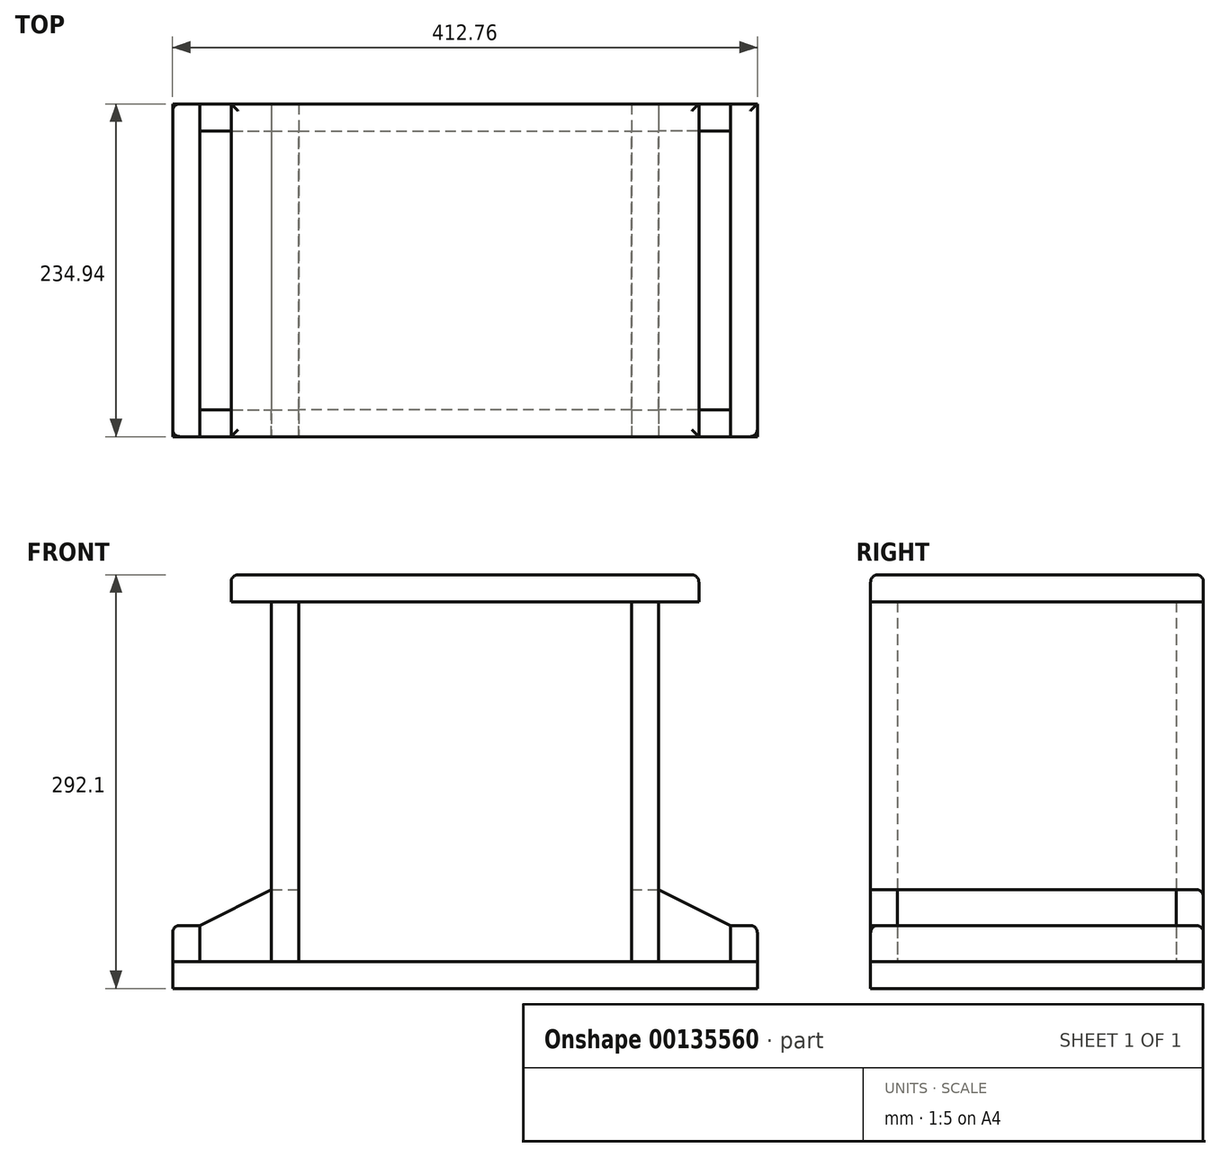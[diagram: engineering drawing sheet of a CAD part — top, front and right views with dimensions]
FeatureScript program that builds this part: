
annotation { "Feature Type Name" : "Feature", "Feature Type Description" : "" }
export const myFeature = defineFeature(function(context is Context, id is Id, definition is map)
    precondition{}
    {
        {
            var Q0;
            Q0=qCreatedBy(makeId("Top.planeOp"),FACE);
            var sketch = newSketch(context, id + "F0", { "sketchPlane" : qUnion([Q0])});
            skLineSegment(sketch, "E0.bottom", {"start": v(206.38, -117.47) * mm, "end": v(-206.38, -117.48) * mm});
            skLineSegment(sketch, "E0.top", {"start": v(206.38, 117.48) * mm, "end": v(-206.38, 117.47) * mm});
            skLineSegment(sketch, "E0.left", {"start": v(206.38, -117.47) * mm, "end": v(206.38, 117.48) * mm});
            skLineSegment(sketch, "E0.right", {"start": v(-206.38, -117.48) * mm, "end": v(-206.38, 117.48) * mm});
            skPoint(sketch, "E0.middle", {"position": v(0, 0) * mm});
            skSolve(sketch);
        }
        {
            var Q0;
            Q0 = qSketchRegion(id + "F0", true);
            extrude(context, id + "F1", {"entities" : qUnion([Q0]), "depth" : 19.05 * mm});
        }
        {
            var Q0;
            Q0=makeQuery(id+"F1.opExtrude","CAP_FACE",FACE,{"disambiguationData":[OSD([sQuery(id+"F0.wireOp",EDGE,"E0.bottom"),sQuery(id+"F0.wireOp",EDGE,"E0.top"),sQuery(id+"F0.wireOp",EDGE,"E0.left"),sQuery(id+"F0.wireOp",EDGE,"E0.right")])],"isStart":false});
            var sketch = newSketch(context, id + "F2", { "sketchPlane" : qUnion([Q0])});
            skLineSegment(sketch, "E1.bottom", {"start": v(-206.38, 117.48) * mm, "end": v(-187.33, 117.48) * mm});
            skLineSegment(sketch, "E1.top", {"start": v(-206.38, -117.48) * mm, "end": v(-187.33, -117.48) * mm});
            skLineSegment(sketch, "E1.left", {"start": v(-206.38, 117.48) * mm, "end": v(-206.38, -117.48) * mm});
            skLineSegment(sketch, "E1.right", {"start": v(-187.33, 117.48) * mm, "end": v(-187.33, -117.48) * mm});
            skLineSegment(sketch, "E2.bottom", {"start": v(206.38, 117.48) * mm, "end": v(187.33, 117.48) * mm});
            skLineSegment(sketch, "E2.top", {"start": v(206.38, -117.47) * mm, "end": v(187.33, -117.47) * mm});
            skLineSegment(sketch, "E2.left", {"start": v(206.38, 117.48) * mm, "end": v(206.38, -117.47) * mm});
            skLineSegment(sketch, "E2.right", {"start": v(187.33, 117.48) * mm, "end": v(187.33, -117.47) * mm});
            skSolve(sketch);
        }
        {
            var Q0;
            Q0 = qSketchRegion(id + "F2", true);
            extrude(context, id + "F3", {"entities" : qUnion([Q0]), "depth" : 25.4 * mm});
        }
        {
            var Q0;
            Q0=makeQuery(id+"F1.opExtrude","CAP_FACE",FACE,{"disambiguationData":[OSD([sQuery(id+"F0.wireOp",EDGE,"E0.bottom"),sQuery(id+"F0.wireOp",EDGE,"E0.top"),sQuery(id+"F0.wireOp",EDGE,"E0.left"),sQuery(id+"F0.wireOp",EDGE,"E0.right")])],"isStart":false});
            var sketch = newSketch(context, id + "F4", { "sketchPlane" : qUnion([Q0])});
            skLineSegment(sketch, "E3.bottom", {"start": v(-187.33, 117.47) * mm, "end": v(-136.53, 117.47) * mm});
            skLineSegment(sketch, "E3.top", {"start": v(-187.33, 98.42) * mm, "end": v(-136.53, 98.42) * mm});
            skLineSegment(sketch, "E3.left", {"start": v(-187.33, 117.47) * mm, "end": v(-187.33, 98.42) * mm});
            skLineSegment(sketch, "E3.right", {"start": v(-136.53, 117.47) * mm, "end": v(-136.53, 98.42) * mm});
            skLineSegment(sketch, "E4.bottom", {"start": v(-187.33, -117.48) * mm, "end": v(-136.53, -117.48) * mm});
            skLineSegment(sketch, "E4.top", {"start": v(-187.33, -98.43) * mm, "end": v(-136.53, -98.43) * mm});
            skLineSegment(sketch, "E4.left", {"start": v(-187.33, -117.48) * mm, "end": v(-187.33, -98.43) * mm});
            skLineSegment(sketch, "E4.right", {"start": v(-136.53, -117.48) * mm, "end": v(-136.53, -98.43) * mm});
            skSolve(sketch);
        }
        {
            var Q0;
            Q0 = qSketchRegion(id + "F4", true);
            extrude(context, id + "F5", {"entities" : qUnion([Q0]), "depth" : 50.8 * mm});
        }
        {
            var Q0;
            Q0=makeQuery(id+"F1.opExtrude","CAP_FACE",FACE,{"disambiguationData":[OSD([sQuery(id+"F0.wireOp",EDGE,"E0.bottom"),sQuery(id+"F0.wireOp",EDGE,"E0.top"),sQuery(id+"F0.wireOp",EDGE,"E0.left"),sQuery(id+"F0.wireOp",EDGE,"E0.right")])],"isStart":false});
            var sketch = newSketch(context, id + "F6", { "sketchPlane" : qUnion([Q0])});
            skLineSegment(sketch, "E5.bottom", {"start": v(-136.53, 117.48) * mm, "end": v(-117.48, 117.48) * mm});
            skLineSegment(sketch, "E5.top", {"start": v(-136.53, -117.48) * mm, "end": v(-117.48, -117.48) * mm});
            skLineSegment(sketch, "E5.left", {"start": v(-136.53, 117.48) * mm, "end": v(-136.53, -117.48) * mm});
            skLineSegment(sketch, "E5.right", {"start": v(-117.48, 117.48) * mm, "end": v(-117.48, -117.48) * mm});
            skLineSegment(sketch, "E6.bottom", {"start": v(136.53, 117.48) * mm, "end": v(117.48, 117.48) * mm});
            skLineSegment(sketch, "E6.top", {"start": v(136.53, -117.47) * mm, "end": v(117.48, -117.47) * mm});
            skLineSegment(sketch, "E6.left", {"start": v(136.53, 117.48) * mm, "end": v(136.53, -117.47) * mm});
            skLineSegment(sketch, "E6.right", {"start": v(117.48, 117.48) * mm, "end": v(117.48, -117.47) * mm});
            skSolve(sketch);
        }
        {
            var Q0;
            Q0 = qSketchRegion(id + "F6", true);
            extrude(context, id + "F7", {"entities" : qUnion([Q0]), "depth" : 254 * mm});
        }
        {
            var Q0;
            Q0=makeQuery(id+"F7.opExtrude","SWEPT_FACE",FACE,{"disambiguationData":[OSD([sQuery(id+"F6.wireOp",EDGE,"E6.left")])]});
            var sketch = newSketch(context, id + "F8", { "sketchPlane" : qUnion([Q0])});
            skLineSegment(sketch, "E7.bottom", {"start": v(-98.43, 19.05) * mm, "end": v(98.42, 19.05) * mm});
            skLineSegment(sketch, "E7.top", {"start": v(-98.43, 69.85) * mm, "end": v(98.42, 69.85) * mm});
            skLineSegment(sketch, "E7.left", {"start": v(-98.43, 19.05) * mm, "end": v(-98.43, 69.85) * mm});
            skLineSegment(sketch, "E7.right", {"start": v(98.42, 19.05) * mm, "end": v(98.42, 69.85) * mm});
            skSolve(sketch);
        }
        {
            var Q0;
            Q0 = qSketchRegion(id + "F8", true);
            var Q1;
            Q1=makeQuery(id+"F7.opExtrude","SWEPT_FACE",FACE,{"disambiguationData":[OSD([sQuery(id+"F6.wireOp",EDGE,"E5.left")])]});
            extrude(context, id + "F9", {"entities" : qUnion([Q0]), "operationType" : NewBodyOperationType.REMOVE, "endBound" : BoundingType.UP_TO_SURFACE, "oppositeDirection" : true, "endBoundEntityFace" : qUnion([Q1]), "depth" : 25.4 * mm});
        }
        {
            var Q0;
            Q0=makeQuery(id+"F1.opExtrude","CAP_FACE",FACE,{"disambiguationData":[OSD([sQuery(id+"F0.wireOp",EDGE,"E0.bottom"),sQuery(id+"F0.wireOp",EDGE,"E0.top"),sQuery(id+"F0.wireOp",EDGE,"E0.left"),sQuery(id+"F0.wireOp",EDGE,"E0.right")])],"isStart":false});
            var sketch = newSketch(context, id + "F10", { "sketchPlane" : qUnion([Q0])});
            skLineSegment(sketch, "E8.bottom", {"start": v(-117.48, 117.48) * mm, "end": v(117.47, 117.48) * mm});
            skLineSegment(sketch, "E8.top", {"start": v(-117.48, 98.43) * mm, "end": v(117.47, 98.43) * mm});
            skLineSegment(sketch, "E8.left", {"start": v(-117.48, 117.48) * mm, "end": v(-117.48, 98.43) * mm});
            skLineSegment(sketch, "E8.right", {"start": v(117.47, 117.48) * mm, "end": v(117.47, 98.43) * mm});
            skLineSegment(sketch, "E9.bottom", {"start": v(117.47, -117.47) * mm, "end": v(-117.48, -117.48) * mm});
            skLineSegment(sketch, "E9.top", {"start": v(117.47, -98.42) * mm, "end": v(-117.48, -98.43) * mm});
            skLineSegment(sketch, "E9.left", {"start": v(117.47, -117.47) * mm, "end": v(117.47, -98.42) * mm});
            skLineSegment(sketch, "E9.right", {"start": v(-117.48, -117.48) * mm, "end": v(-117.48, -98.43) * mm});
            skSolve(sketch);
        }
        {
            var Q0;
            Q0 = qSketchRegion(id + "F10", true);
            extrude(context, id + "F11", {"entities" : qUnion([Q0]), "depth" : 254 * mm});
        }
        {
            var Q0;
            Q0=makeQuery(id+"F11.opExtrude","CAP_FACE",FACE,{"disambiguationData":[OSD([sQuery(id+"F10.wireOp",EDGE,"E8.bottom"),sQuery(id+"F10.wireOp",EDGE,"E8.top"),sQuery(id+"F10.wireOp",EDGE,"E8.left"),sQuery(id+"F10.wireOp",EDGE,"E8.right")])],"isStart":false});
            var sketch = newSketch(context, id + "F12", { "sketchPlane" : qUnion([Q0])});
            skLineSegment(sketch, "E10.bottom", {"start": v(165.1, -117.48) * mm, "end": v(-165.1, -117.48) * mm});
            skLineSegment(sketch, "E10.top", {"start": v(165.1, 117.48) * mm, "end": v(-165.1, 117.48) * mm});
            skLineSegment(sketch, "E10.left", {"start": v(165.1, -117.48) * mm, "end": v(165.1, 117.48) * mm});
            skLineSegment(sketch, "E10.right", {"start": v(-165.1, -117.48) * mm, "end": v(-165.1, 117.48) * mm});
            skPoint(sketch, "E10.middle", {"position": v(0, 0) * mm});
            skSolve(sketch);
        }
        {
            var Q0;
            Q0 = qSketchRegion(id + "F12", true);
            extrude(context, id + "F13", {"entities" : qUnion([Q0]), "depth" : 19.05 * mm});
        }
        {
            var Q0;
            Q0=makeQuery(id+"F5.opExtrude","SWEPT_FACE",FACE,{"disambiguationData":[OSD([sQuery(id+"F4.wireOp",EDGE,"E4.bottom")])]});
            var sketch = newSketch(context, id + "F14", { "sketchPlane" : qUnion([Q0])});
            skLineSegment(sketch, "E11", {"start": v(-136.53, 69.85) * mm, "end": v(-187.33, 44.45) * mm});
            skLineSegment(sketch, "E12", {"start": v(-187.33, 44.45) * mm, "end": v(-187.33, 69.85) * mm});
            skLineSegment(sketch, "E13", {"start": v(-187.33, 69.85) * mm, "end": v(-136.53, 69.85) * mm});
            skSolve(sketch);
        }
        {
            var Q0;
            Q0 = qSketchRegion(id + "F14", true);
            extrude(context, id + "F15", {"entities" : qUnion([Q0]), "operationType" : NewBodyOperationType.REMOVE, "endBound" : BoundingType.THROUGH_ALL, "oppositeDirection" : true, "depth" : 25.4 * mm});
        }
        {
            var Q0;
            Q0=makeQuery(id+"F3.opExtrude","CAP_EDGE",EDGE,{"disambiguationData":[OSD([sQuery(id+"F2.wireOp",EDGE,"E1.left")])],"isStart":false});
            var Q1;
            Q1=makeQuery(id+"F3.opExtrude","CAP_EDGE",EDGE,{"disambiguationData":[OSD([sQuery(id+"F2.wireOp",EDGE,"E2.left")])],"isStart":false});
            var Q2;
            Q2=makeQuery(id+"F3.opExtrude","CAP_EDGE",EDGE,{"disambiguationData":[OSD([sQuery(id+"F2.wireOp",EDGE,"E2.bottom")])],"isStart":false});
            var Q3;
            Q3=makeQuery(id+"F3.opExtrude","CAP_EDGE",EDGE,{"disambiguationData":[OSD([sQuery(id+"F2.wireOp",EDGE,"E1.bottom")])],"isStart":false});
            var Q4;
            Q4=makeQuery(id+"F3.opExtrude","SWEPT_EDGE",EDGE,{"disambiguationData":[OSD([sQuery(id+"F2.wireOp",EDGE,"E1.top"),sQuery(id+"F2.wireOp",EDGE,"E1.left")])]});
            var Q5;
            Q5=makeQuery(id+"F3.opExtrude","SWEPT_EDGE",EDGE,{"disambiguationData":[OSD([sQuery(id+"F2.wireOp",EDGE,"E1.bottom"),sQuery(id+"F2.wireOp",EDGE,"E1.left")])]});
            var Q6;
            Q6=makeQuery(id+"F3.opExtrude","SWEPT_EDGE",EDGE,{"disambiguationData":[OSD([sQuery(id+"F2.wireOp",EDGE,"E2.top"),sQuery(id+"F2.wireOp",EDGE,"E2.left")])]});
            var Q7;
            Q7=makeQuery(id+"F3.opExtrude","CAP_EDGE",EDGE,{"disambiguationData":[OSD([sQuery(id+"F2.wireOp",EDGE,"E2.top")])],"isStart":false});
            var Q8;
            Q8=makeQuery(id+"F3.opExtrude","CAP_EDGE",EDGE,{"disambiguationData":[OSD([sQuery(id+"F2.wireOp",EDGE,"E1.top")])],"isStart":false});
            var Q9;
            Q9=makeQuery(id+"F15.boolean.opBoolean","INTERSECT",EDGE,{"derivedFrom":[makeQuery(id+"F5.opExtrude","SWEPT_FACE",FACE,{"disambiguationData":[OSD([sQuery(id+"F4.wireOp",EDGE,"E3.bottom")])]}),makeQuery(id+"F15.opExtrude","SWEPT_FACE",FACE,{"disambiguationData":[OSD([sQuery(id+"F14.wireOp",EDGE,"E11")])]})]});
            var Q10;
            Q10=makeQuery(id+"F15.boolean.opBoolean","COPY",EDGE,{"derivedFrom":makeQuery(id+"F15.opExtrude","CAP_EDGE",EDGE,{"disambiguationData":[OSD([sQuery(id+"F14.wireOp",EDGE,"E11")])],"isStart":true})});
            var Q11;
            Q11=makeQuery(id+"F13.opExtrude","CAP_EDGE",EDGE,{"disambiguationData":[OSD([sQuery(id+"F12.wireOp",EDGE,"E10.top")])],"isStart":false});
            var Q12;
            Q12=makeQuery(id+"F13.opExtrude","CAP_EDGE",EDGE,{"disambiguationData":[OSD([sQuery(id+"F12.wireOp",EDGE,"E10.right")])],"isStart":false});
            var Q13;
            Q13=makeQuery(id+"F13.opExtrude","CAP_EDGE",EDGE,{"disambiguationData":[OSD([sQuery(id+"F12.wireOp",EDGE,"E10.bottom")])],"isStart":false});
            var Q14;
            Q14=makeQuery(id+"F13.opExtrude","CAP_EDGE",EDGE,{"disambiguationData":[OSD([sQuery(id+"F12.wireOp",EDGE,"E10.left")])],"isStart":false});
            fillet(context, id + "F16", {"entities" : qUnion([Q0, Q1, Q2, Q3, Q4, Q5, Q6, Q7, Q8, Q9, Q10, Q11, Q12, Q13, Q14]), "radius" : 5.08 * mm, "tangentPropagation" : true, "allowEdgeOverflow" : false});
        }
        {
            var Q0;
            Q0=makeQuery(id+"F5.opExtrude","SWEPT_BODY",BODY,{"disambiguationData":[OSD([sQuery(id+"F4.wireOp",EDGE,"E4.bottom"),sQuery(id+"F4.wireOp",EDGE,"E4.top"),sQuery(id+"F4.wireOp",EDGE,"E4.left"),sQuery(id+"F4.wireOp",EDGE,"E4.right")])]});
            var Q1;
            Q1=makeQuery(id+"F5.opExtrude","SWEPT_BODY",BODY,{"disambiguationData":[OSD([sQuery(id+"F4.wireOp",EDGE,"E3.bottom"),sQuery(id+"F4.wireOp",EDGE,"E3.top"),sQuery(id+"F4.wireOp",EDGE,"E3.left"),sQuery(id+"F4.wireOp",EDGE,"E3.right")])]});
            var Q2;
            Q2=qCreatedBy(makeId("Right.planeOp"),FACE);
            mirror(context, id + "F17", {"entities" : qUnion([Q0, Q1]), "mirrorPlane" : qUnion([Q2])});
        }
    });
